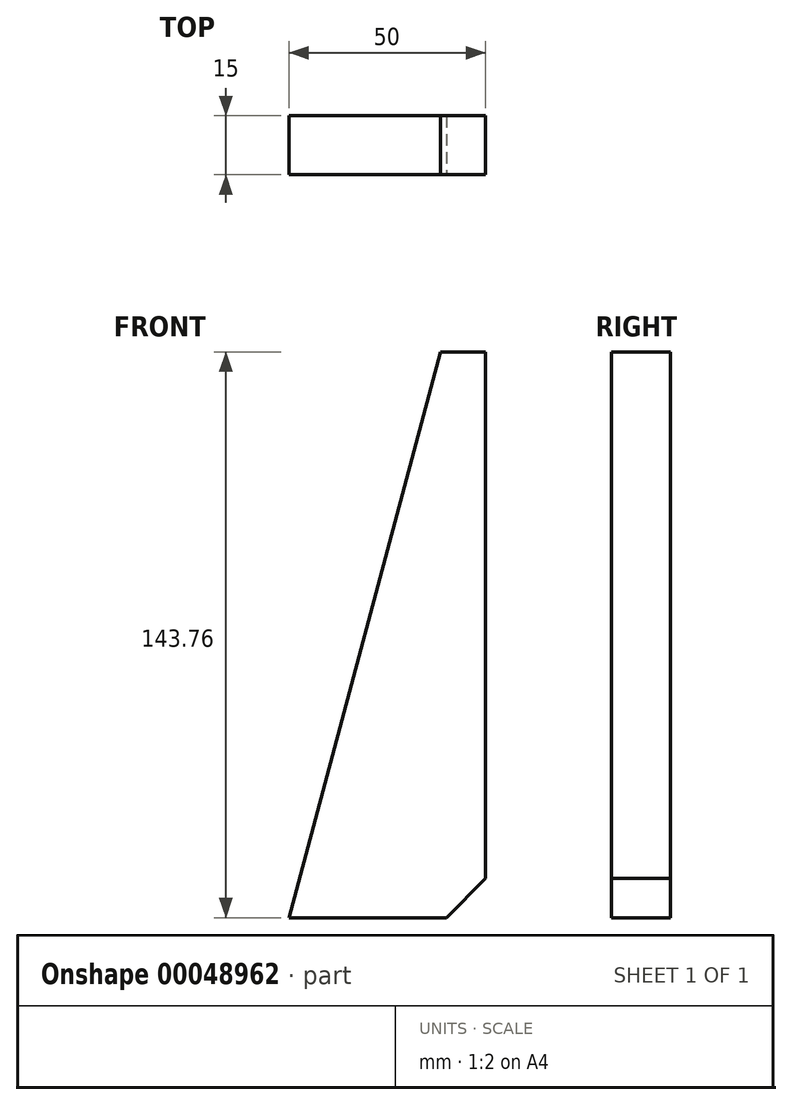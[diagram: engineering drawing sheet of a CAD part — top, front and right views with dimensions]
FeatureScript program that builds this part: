
annotation { "Feature Type Name" : "Feature", "Feature Type Description" : "" }
export const myFeature = defineFeature(function(context is Context, id is Id, definition is map)
    precondition{}
    {
        {
            var Q0;
            Q0=qCreatedBy(makeId("Front.planeOp"),FACE);
            var sketch = newSketch(context, id + "F0", { "sketchPlane" : qUnion([Q0])});
            skLineSegment(sketch, "E0", {"start": v(-78.69, -70.35) * mm, "end": v(-40.16, 73.41) * mm});
            skLineSegment(sketch, "E1", {"start": v(-78.69, -70.35) * mm, "end": v(-28.69, -70.35) * mm});
            skLineSegment(sketch, "E2", {"start": v(-28.69, 73.41) * mm, "end": v(-40.16, 73.41) * mm});
            skLineSegment(sketch, "E3", {"start": v(-28.69, 73.41) * mm, "end": v(-28.69, -70.35) * mm});
            skSolve(sketch);
        }
        {
            var Q0;
            Q0=makeQuery(id+"F0.imprint","IMPRINT",FACE,{"disambiguationData":[TD([[makeQuery(id+"F0.imprint","IMPRINT",EDGE,{"derivedFrom":sQuery(id+"F0.wireOp",EDGE,"E0")}),-1.0]])]});
            extrude(context, id + "F1", {"entities" : qUnion([Q0]), "depth" : 15 * mm});
        }
        {
            var Q0;
            Q0=makeQuery(id+"F1.opExtrude","SWEPT_EDGE",EDGE,{"disambiguationData":[OSD([sQuery(id+"F0.wireOp",EDGE,"E1"),sQuery(id+"F0.wireOp",EDGE,"E3")])]});
            chamfer(context, id + "F2", {"entities" : qUnion([Q0]), "width" : 10 * mm, "tangentPropagation" : true});
        }
    });
